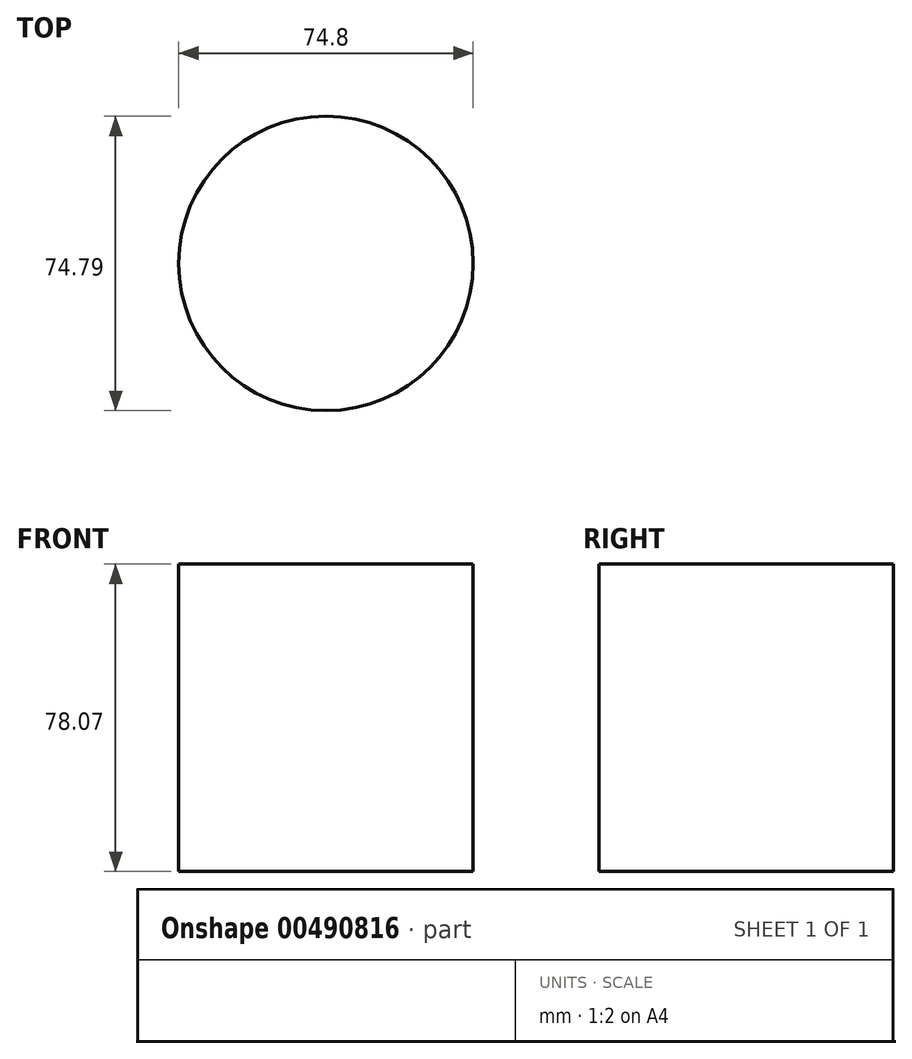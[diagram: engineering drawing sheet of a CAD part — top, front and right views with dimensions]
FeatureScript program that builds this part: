
annotation { "Feature Type Name" : "Feature", "Feature Type Description" : "" }
export const myFeature = defineFeature(function(context is Context, id is Id, definition is map)
    precondition{}
    {
        {
            var Q0;
            Q0=qCreatedBy(makeId("Top.planeOp"),FACE);
            var sketch = newSketch(context, id + "F0", { "sketchPlane" : qUnion([Q0])});
            skCircle(sketch, "E0", {"center": v(0, 0) * mm, "radius": 35.03 * mm});
            skCircle(sketch, "E1", {"center": v(34.83, 3.72) * mm, "radius": 37.4 * mm});
            skCircle(sketch, "E2", {"center": v(69.5, -10.31) * mm, "radius": 17.5 * mm});
            skSolve(sketch);
        }
        {
            var Q0;
            Q0=sQuery(id+"F0.wireOp",EDGE,"E1");
            extrude(context, id + "F1", {"bodyType" : ToolBodyType.SURFACE, "surfaceEntities" : qUnion([Q0]), "depth" : 78.07 * mm});
        }
    });
